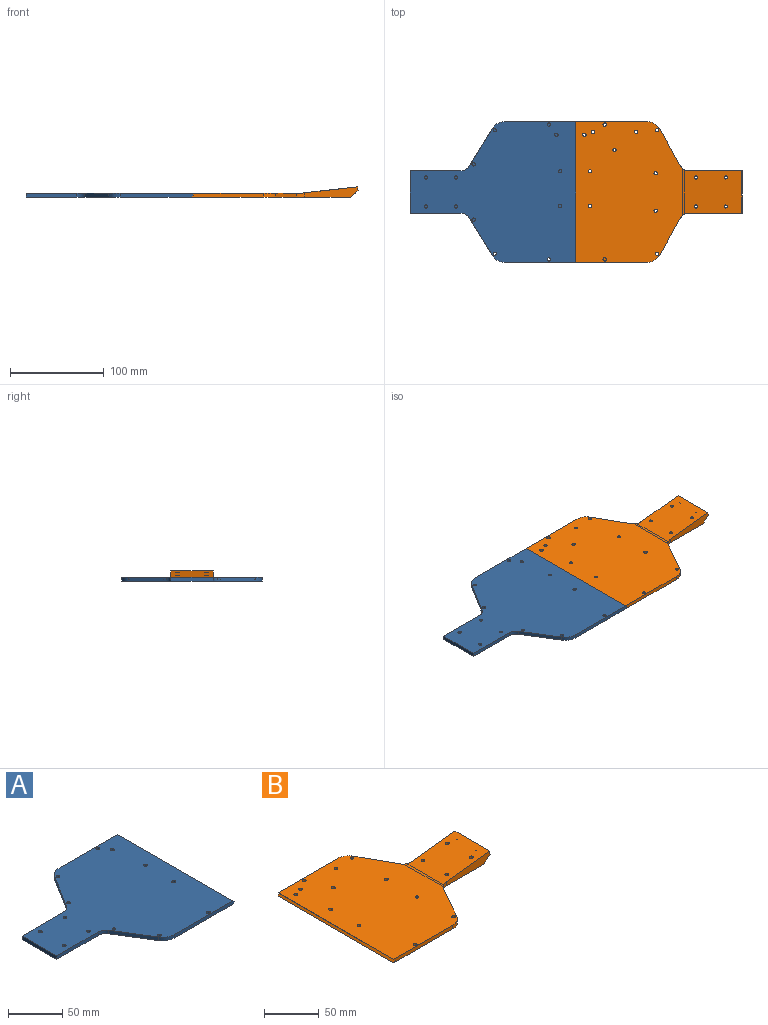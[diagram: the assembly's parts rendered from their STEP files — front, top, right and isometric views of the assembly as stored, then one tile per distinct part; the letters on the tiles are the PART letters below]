
ASSEMBLY  parts=2 mates=1
PART A: 41 faces, bbox 178.9x150x4 mm
  f0: cylinder r=1.75mm len=3.5mm, axis (0,0,-1), area 27.5mm2, adj f1,f25
  f1: cone r=1.75mm half-angle=45deg, axis (0,0,-1), area 33.3mm2, adj f0,f2
  f2: plane 176.89x150mm, normal (0,0,-1), area 18113.7mm2, adj f1,f4,f6,f8,f10,f12,f14,f16
  f3: plane 150x2mm, normal (0.71,0,0.71), area 424.3mm2, adj f4,f25,f27,f28
  f4: plane 150x2mm, normal (0.71,0,-0.71), area 424.3mm2, adj f2,f3,f27,f28
  f5: cylinder r=1.75mm len=3.5mm, axis (0,0,-1), area 30.2mm2, adj f6,f25
  f6: cone r=1.75mm half-angle=45deg, axis (0,0,-1), area 26.4mm2, adj f2,f5
  f7: cylinder r=1.75mm len=3.5mm, axis (0,0,-1), area 30.2mm2, adj f8,f25
  f8: cone r=1.75mm half-angle=45deg, axis (0,0,-1), area 26.4mm2, adj f2,f7
  f9: cylinder r=1.75mm len=3.5mm, axis (0,0,-1), area 30.2mm2, adj f10,f25
  f10: cone r=1.75mm half-angle=45deg, axis (0,0,-1), area 26.4mm2, adj f2,f9
  f11: cylinder r=1.75mm len=3.5mm, axis (0,0,-1), area 30.2mm2, adj f12,f25
  f12: cone r=1.75mm half-angle=45deg, axis (0,0,-1), area 26.4mm2, adj f2,f11
  f13: cylinder r=1.75mm len=3.5mm, axis (0,0,-1), area 30.2mm2, adj f14,f25
  f14: cone r=1.75mm half-angle=45deg, axis (0,0,-1), area 26.4mm2, adj f2,f13
  f15: cylinder r=1.75mm len=3.5mm, axis (0,0,-1), area 30.2mm2, adj f16,f25
  f16: cone r=1.75mm half-angle=45deg, axis (0,0,-1), area 26.4mm2, adj f2,f15
  f17: cylinder r=1.75mm len=3.5mm, axis (0,0,-1), area 27.5mm2, adj f18,f25
  f18: cone r=1.75mm half-angle=45deg, axis (0,0,-1), area 33.3mm2, adj f2,f17
  f19: cylinder r=1.75mm len=3.5mm, axis (0,0,-1), area 27.5mm2, adj f20,f25
  f20: cone r=1.75mm half-angle=45deg, axis (0,0,-1), area 33.3mm2, adj f2,f19
  f21: cylinder r=1.75mm len=3.5mm, axis (0,0,-1), area 27.5mm2, adj f22,f25
  f22: cone r=1.75mm half-angle=45deg, axis (0,0,-1), area 33.3mm2, adj f2,f21
  f23: cylinder r=1.75mm len=3.5mm, axis (0,0,-1), area 27.5mm2, adj f24,f25
  f24: cone r=1.75mm half-angle=45deg, axis (0,0,-1), area 33.3mm2, adj f2,f23
  f25: plane 176.89x150mm, normal (0,0,1), area 18390.6mm2, adj f0,f3,f5,f7,f9,f11,f13,f15
  f26: plane 40.66x25.17mm, normal (-0.85,-0.53,0), area 191.3mm2, adj f2,f25,f33,f35
  f27: plane 78.04x4mm, normal (0,-1,0), area 308.2mm2, adj f2,f3,f4,f25,f33
  f28: plane 78.04x4mm, normal (0,1,0), area 308.2mm2, adj f2,f3,f4,f25,f34
  f29: plane 40.66x25.17mm, normal (-0.85,0.53,0), area 191.3mm2, adj f2,f25,f34,f36
  f30: plane 54.43x4mm, normal (0,1,0), area 217.7mm2, adj f2,f25,f31,f36
  f31: plane 45x4mm, normal (-1,0,0), area 180mm2, adj f2,f25,f30,f32
  f32: plane 54.43x4mm, normal (0,-1,0), area 217.7mm2, adj f2,f25,f31,f35
  f33: cylinder r=15mm len=12.75mm, axis (0,0,-1), area 61mm2, adj f2,f25,f26,f27
  f34: cylinder r=15mm len=12.75mm, axis (0,0,-1), area 61mm2, adj f2,f25,f28,f29
  f35: cylinder r=10mm len=8.5mm, axis (0,0,1), area 40.7mm2, adj f2,f25,f26,f32
  f36: cylinder r=10mm len=8.5mm, axis (0,0,1), area 40.7mm2, adj f2,f25,f29,f30
  f37: cone r=1.75mm half-angle=45deg, axis (0,0,-1), area 33.3mm2, adj f2,f38
  f38: cylinder r=1.75mm len=3.5mm, axis (0,0,-1), area 27.5mm2, adj f25,f37
  f39: cylinder r=1.75mm len=3.5mm, axis (0,0,-1), area 27.5mm2, adj f25,f40
  f40: cone r=1.75mm half-angle=45deg, axis (0,0,-1), area 33.3mm2, adj f2,f39
PART B: 58 faces, bbox 177.6x150x11.8 mm
  f0: cylinder r=10mm len=8.72mm, axis (0,0,1), area 44.5mm2, adj f17,f19,f20,f25,f27,f57
  f1: cylinder r=10mm len=8.72mm, axis (0,0,1), area 44.5mm2, adj f17,f21,f22,f25,f27,f57
  f2: cone r=1.75mm half-angle=45deg, axis (0,0,-1), area 26.4mm2, adj f25,f34,f56
  f3: cylinder r=1.75mm len=3.5mm, axis (0,0,-1), area 30.2mm2, adj f4,f27
  f4: cone r=1.75mm half-angle=45deg, axis (0,0,-1), area 26.4mm2, adj f3,f25
  f5: plane 7x6.96mm, normal (0.11,0,-0.99), area 29.9mm2, adj f6,f13
  f6: cylinder r=3.5mm len=7.17mm, axis (-0.11,0,0.99), area 34.2mm2, adj f5,f25
  f7: plane 7x6.96mm, normal (0.11,0,-0.99), area 29.9mm2, adj f8,f16
  f8: cylinder r=3.5mm len=7.58mm, axis (-0.11,0,0.99), area 113.4mm2, adj f7,f25
  f9: plane 7x6.96mm, normal (0.11,0,-0.99), area 29.9mm2, adj f10,f15
  f10: cylinder r=3.5mm len=7.58mm, axis (-0.11,0,0.99), area 113.4mm2, adj f9,f25
  f11: plane 7x6.96mm, normal (0.11,0,-0.99), area 29.9mm2, adj f12,f14
  f12: cylinder r=3.5mm len=7.17mm, axis (-0.11,0,0.99), area 34.2mm2, adj f11,f25
  f13: cylinder r=1.65mm len=4.34mm, axis (-0.11,0,0.99), area 41.5mm2, adj f5,f17
  f14: cylinder r=1.65mm len=4.34mm, axis (-0.11,0,0.99), area 41.5mm2, adj f11,f17
  f15: cylinder r=1.65mm len=4.34mm, axis (-0.11,0,0.99), area 41.5mm2, adj f9,f17
  f16: cylinder r=1.65mm len=4.34mm, axis (-0.11,0,0.99), area 41.5mm2, adj f7,f17
  f17: plane 61.11x47.4mm, normal (-0.11,0,0.99), area 2736.2mm2, adj f0,f1,f13,f14,f15,f16,f18,f20
  f18: plane 45x3.98mm, normal (0.99,0,0.11), area 180mm2, adj f17,f20,f21,f24
  f19: plane 39.75x22.33mm, normal (0.87,-0.49,0), area 182.4mm2, adj f0,f25,f27,f56
  f20: plane 56.81x11mm, normal (0,-1,0), area 415.9mm2, adj f0,f17,f18,f24,f25
  f21: plane 56.81x11mm, normal (0,1,0), area 415.9mm2, adj f1,f17,f18,f24,f25
  f22: plane 39.75x22.33mm, normal (0.87,0.49,0), area 182.4mm2, adj f1,f25,f27,f55
  f23: plane 76.62x4mm, normal (0,1,0), area 302.5mm2, adj f25,f27,f28,f29,f55
  f24: plane 45x8.37mm, normal (0.64,0,-0.77), area 480.4mm2, adj f18,f20,f21,f25,f41,f43
  f25: plane 169.18x150mm, normal (0,0,-1), area 17580.9mm2, adj f0,f1,f2,f4,f6,f8,f10,f12
  f26: plane 76.62x4mm, normal (0,-1,0), area 302.5mm2, adj f25,f27,f28,f29,f56
  f27: plane 150x113.77mm, normal (0,0,1), area 15493.2mm2, adj f0,f1,f3,f19,f22,f23,f26,f28
  f28: plane 150x2mm, normal (-0.71,0,-0.71), area 424.3mm2, adj f23,f26,f27,f29
  f29: plane 150x2mm, normal (-0.71,0,0.71), area 424.3mm2, adj f23,f25,f26,f28
  f30: cylinder r=1.75mm len=3.5mm, axis (0,0,-1), area 30.2mm2, adj f27,f31
  f31: cone r=1.75mm half-angle=45deg, axis (0,0,-1), area 26.4mm2, adj f25,f30,f55
  f32: cylinder r=1.75mm len=3.5mm, axis (0,0,-1), area 30.2mm2, adj f27,f33
  f33: cone r=1.75mm half-angle=45deg, axis (0,0,-1), area 26.4mm2, adj f25,f32
  f34: cylinder r=1.75mm len=3.5mm, axis (0,0,-1), area 30.2mm2, adj f2,f27
  f35: cylinder r=1.75mm len=3.5mm, axis (0,0,-1), area 27.5mm2, adj f27,f36
  f36: cone r=1.75mm half-angle=45deg, axis (0,0,-1), area 33.3mm2, adj f25,f35
  f37: cone r=1.75mm half-angle=45deg, axis (0,0,-1), area 33.3mm2, adj f25,f54
  f38: cone r=1.75mm half-angle=45deg, axis (0,0,-1), area 33.3mm2, adj f25,f39
  f39: cylinder r=1.75mm len=3.5mm, axis (0,0,-1), area 27.5mm2, adj f27,f38
  f40: plane 2.7x2.07mm, normal (0.64,0,-0.77), area 5.7mm2, adj f41
  f41: cylinder r=1.35mm len=7.1mm, axis (0.64,0,-0.77), area 59.4mm2, adj f24,f40
  f42: plane 2.7x2.07mm, normal (0.64,0,-0.77), area 5.7mm2, adj f43
  f43: cylinder r=1.35mm len=7.1mm, axis (0.64,0,-0.77), area 59.4mm2, adj f24,f42
  f44: cone r=1.75mm half-angle=45deg, axis (0,0,-1), area 33.3mm2, adj f25,f45
  f45: cylinder r=1.75mm len=3.5mm, axis (0,0,-1), area 27.5mm2, adj f27,f44
  f46: cone r=1.75mm half-angle=45deg, axis (0,0,-1), area 33.3mm2, adj f25,f47
  f47: cylinder r=1.75mm len=3.5mm, axis (0,0,-1), area 27.5mm2, adj f27,f46
  f48: cone r=1.75mm half-angle=45deg, axis (0,0,-1), area 33.3mm2, adj f25,f49
  f49: cylinder r=1.75mm len=3.5mm, axis (0,0,-1), area 27.5mm2, adj f27,f48
  f50: cone r=1.75mm half-angle=45deg, axis (0,0,-1), area 33.3mm2, adj f25,f51
  f51: cylinder r=1.75mm len=3.5mm, axis (0,0,-1), area 27.5mm2, adj f27,f50
  f52: cone r=1.75mm half-angle=45deg, axis (0,0,-1), area 33.3mm2, adj f25,f53
  f53: cylinder r=1.75mm len=3.5mm, axis (0,0,-1), area 27.5mm2, adj f27,f52
  f54: cylinder r=1.75mm len=3.5mm, axis (0,0,-1), area 27.5mm2, adj f27,f37
  f55: cylinder r=15mm len=13.08mm, axis (0,0,-1), area 63.5mm2, adj f22,f23,f25,f27,f31
  f56: cylinder r=15mm len=13.08mm, axis (0,0,-1), area 63.5mm2, adj f2,f19,f25,f26,f27
  f57: cylinder r=20mm len=50.66mm, axis (0,-1,0), area 109.9mm2, adj f0,f1,f17,f27
PLACE A t=(0.21,0,0)mm
PLACE B at identity
MATE fastened A.f3 <-> B.f28  axis (0.71,0,0.71) through (-0.39,-75,2)mm
